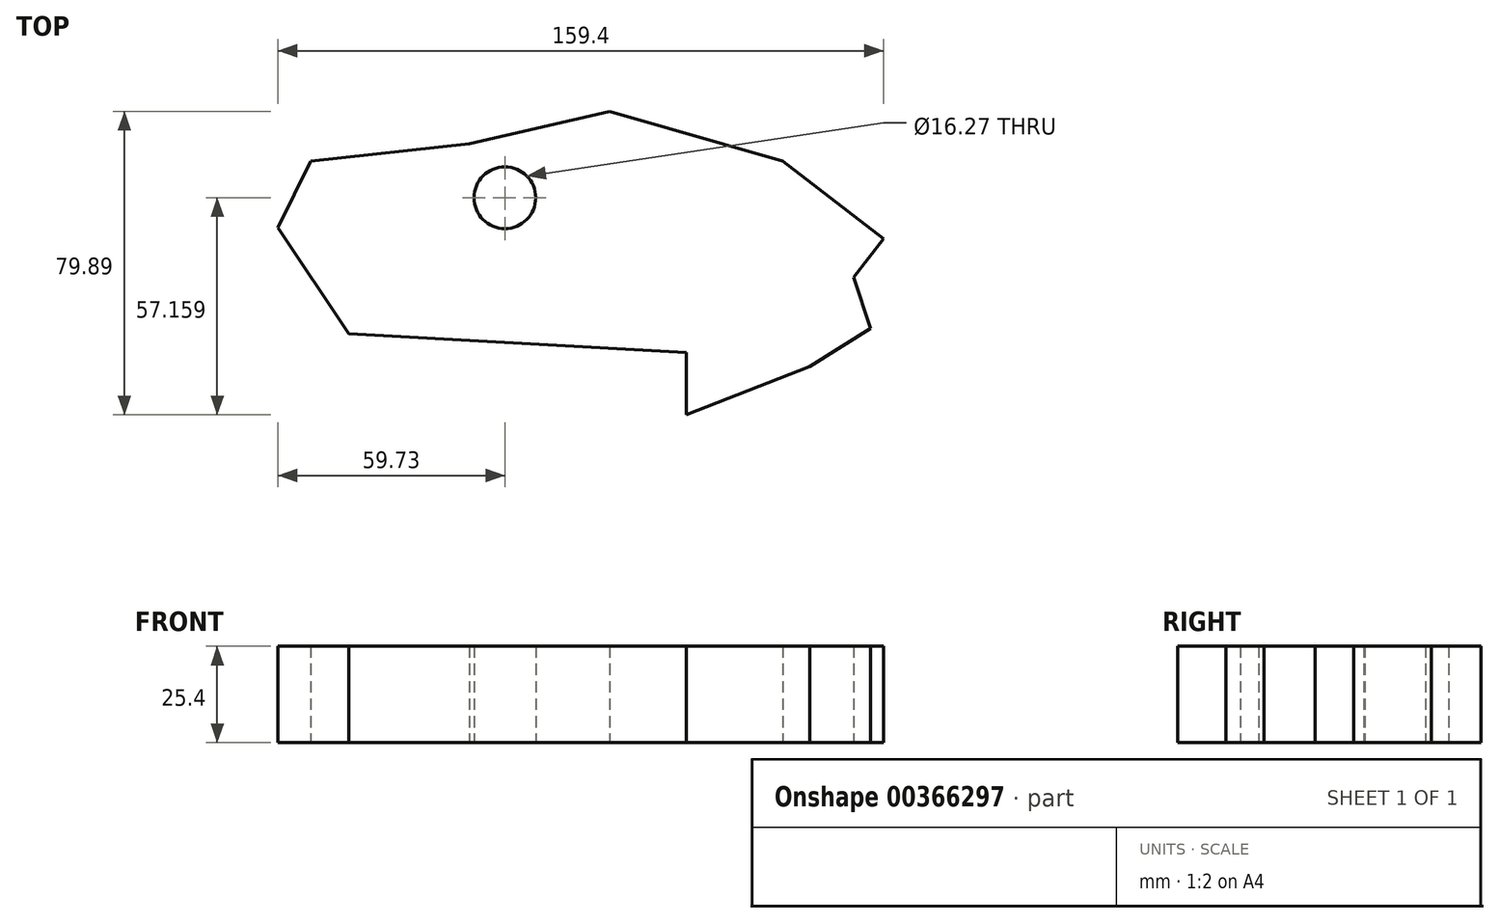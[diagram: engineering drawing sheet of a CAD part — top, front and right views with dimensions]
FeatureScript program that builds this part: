
annotation { "Feature Type Name" : "Feature", "Feature Type Description" : "" }
export const myFeature = defineFeature(function(context is Context, id is Id, definition is map)
    precondition{}
    {
        {
            var Q0;
            Q0=qCreatedBy(makeId("Top.planeOp"),FACE);
            var sketch = newSketch(context, id + "F0", { "sketchPlane" : qUnion([Q0])});
            skLineSegment(sketch, "E0", {"start": v(-41.06, -12.7) * mm, "end": v(-59.73, 15.3) * mm});
            skLineSegment(sketch, "E1", {"start": v(-59.73, 15.3) * mm, "end": v(-51.14, 32.85) * mm});
            skLineSegment(sketch, "E2", {"start": v(-51.14, 32.85) * mm, "end": v(-9.33, 37.33) * mm});
            skLineSegment(sketch, "E3", {"start": v(-9.33, 37.33) * mm, "end": v(27.62, 45.92) * mm});
            skLineSegment(sketch, "E4", {"start": v(27.62, 45.92) * mm, "end": v(73.17, 32.85) * mm});
            skLineSegment(sketch, "E5", {"start": v(73.17, 32.85) * mm, "end": v(99.67, 12.32) * mm});
            skLineSegment(sketch, "E6", {"start": v(99.67, 12.32) * mm, "end": v(91.87, 2.25) * mm});
            skLineSegment(sketch, "E7", {"start": v(91.87, 2.25) * mm, "end": v(96.31, -11.2) * mm});
            skLineSegment(sketch, "E8", {"start": v(96.31, -11.2) * mm, "end": v(80.26, -21.28) * mm});
            skLineSegment(sketch, "E9", {"start": v(80.26, -21.28) * mm, "end": v(47.78, -33.97) * mm});
            skLineSegment(sketch, "E10", {"start": v(47.78, -33.97) * mm, "end": v(47.78, -17.55) * mm});
            skLineSegment(sketch, "E11", {"start": v(47.78, -17.55) * mm, "end": v(-41.06, -12.7) * mm});
            skPoint(sketch, "E12.endSnap0", {"position": v(64.02, -27.62) * mm});
            skCircle(sketch, "E13", {"center": v(0, 23.19) * mm, "radius": 8.13 * mm});
            skSolve(sketch);
        }
        {
            var Q0;
            Q0=makeQuery(id+"F0.imprint","IMPRINT",FACE,{"disambiguationData":[TD([[makeQuery(id+"F0.imprint","IMPRINT",EDGE,{"derivedFrom":sQuery(id+"F0.wireOp",EDGE,"E0")}),-1.0]])]});
            extrude(context, id + "F1", {"entities" : qUnion([Q0]), "depth" : 25.4 * mm});
        }
    });
